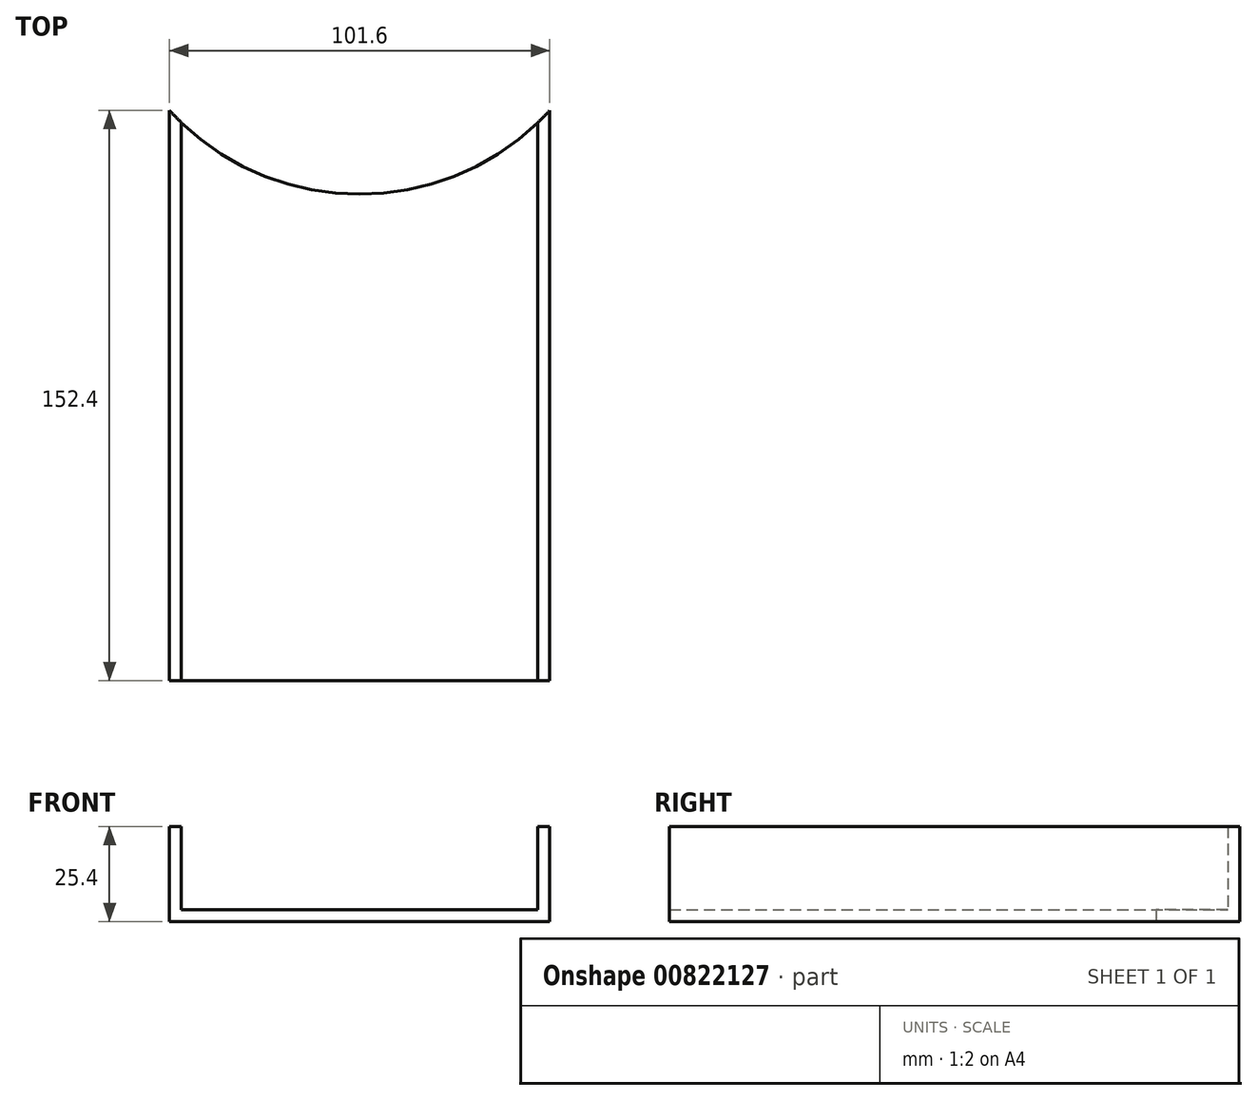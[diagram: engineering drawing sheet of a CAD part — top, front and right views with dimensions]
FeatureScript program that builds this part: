
annotation { "Feature Type Name" : "Feature", "Feature Type Description" : "" }
export const myFeature = defineFeature(function(context is Context, id is Id, definition is map)
    precondition{}
    {
        {
            var Q0;
            Q0=qCreatedBy(makeId("Top.planeOp"),FACE);
            var sketch = newSketch(context, id + "F0", { "sketchPlane" : qUnion([Q0])});
            skLineSegment(sketch, "E0", {"start": v(0, 152.6) * mm, "end": v(0, 0.2) * mm});
            skLineSegment(sketch, "E1", {"start": v(0, 0.2) * mm, "end": v(101.6, 0.2) * mm});
            skLineSegment(sketch, "E2", {"start": v(101.6, 0.2) * mm, "end": v(101.6, 152.6) * mm});
            skArc(sketch, "E3", {"start": v(0, 152.6) * mm, "mid": v(50.8, 130.19) * mm, "end": v(101.6, 152.6) * mm});
            skLineSegment(sketch, "E4", {"start": v(0, 0.2) * mm, "end": v(3.18, 0.2) * mm});
            skLineSegment(sketch, "E5", {"start": v(3.18, 0.2) * mm, "end": v(3.18, 152.6) * mm});
            skLineSegment(sketch, "E6", {"start": v(3.18, 152.6) * mm, "end": v(0, 152.6) * mm});
            skLineSegment(sketch, "E7", {"start": v(101.6, 0.2) * mm, "end": v(98.43, 0.2) * mm});
            skLineSegment(sketch, "E8", {"start": v(98.43, 0.2) * mm, "end": v(98.43, 152.6) * mm});
            skLineSegment(sketch, "E9", {"start": v(98.43, 152.6) * mm, "end": v(101.6, 152.6) * mm});
            skLineSegment(sketch, "E10", {"start": v(3.18, 0.2) * mm, "end": v(3.18, 3.38) * mm});
            skPoint(sketch, "E11.endSnap0", {"position": v(50.8, 0.2) * mm});
            skLineSegment(sketch, "E12", {"start": v(98.43, 3.38) * mm, "end": v(98.43, 0.2) * mm});
            skSolve(sketch);
        }
        {
            var Q0;
            {var subQ0=sQuery(id+"F0.wireOp",EDGE,"E5");var subQ3=makeQuery(id+"F0.imprint","IMPRINT",VERTEX,{"derivedFrom":subQ0});Q0=makeQuery(id+"F0.imprint","IMPRINT",FACE,{"disambiguationData":[TD([[makeQuery(id+"F0.imprint","IMPRINT",EDGE,{"disambiguationData":[TD([[subQ3,-1.0]])],"derivedFrom":subQ0}),-1.0]])]});}
            extrude(context, id + "F1", {"entities" : qUnion([Q0]), "depth" : 3.17 * mm, "offsetDistance" : 25.4 * mm});
        }
        {
            var Q0;
            {var subQ5=sQuery(id+"F0.wireOp",EDGE,"E0");Q0=makeQuery(id+"F0.imprint","IMPRINT",FACE,{"disambiguationData":[TD([[makeQuery(id+"F0.imprint","IMPRINT",EDGE,{"derivedFrom":subQ5}),1.0]])]});}
            extrude(context, id + "F2", {"entities" : qUnion([Q0]), "operationType" : NewBodyOperationType.ADD, "depth" : 25.4 * mm, "offsetDistance" : 25.4 * mm});
        }
        {
            var Q0;
            {var subQ4=sQuery(id+"F0.wireOp",EDGE,"E2");Q0=makeQuery(id+"F0.imprint","IMPRINT",FACE,{"disambiguationData":[TD([[makeQuery(id+"F0.imprint","IMPRINT",EDGE,{"derivedFrom":subQ4}),1.0]])]});}
            extrude(context, id + "F3", {"entities" : qUnion([Q0]), "operationType" : NewBodyOperationType.ADD, "depth" : 25.4 * mm, "offsetDistance" : 25.4 * mm});
        }
    });
